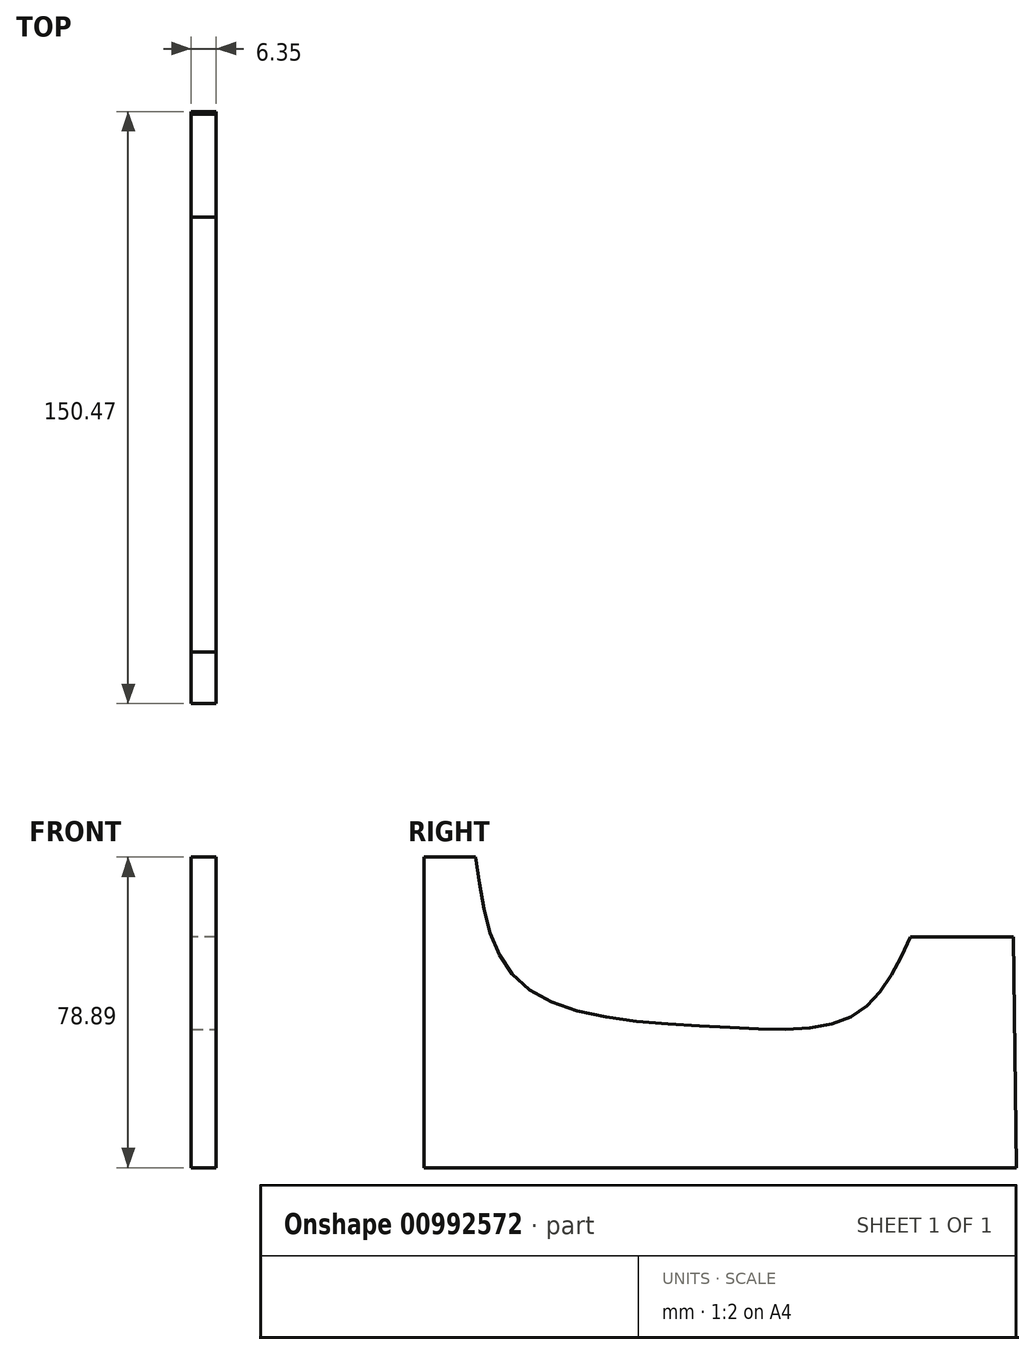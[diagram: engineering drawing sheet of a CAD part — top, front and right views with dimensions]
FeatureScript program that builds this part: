
annotation { "Feature Type Name" : "Feature", "Feature Type Description" : "" }
export const myFeature = defineFeature(function(context is Context, id is Id, definition is map)
    precondition{}
    {
        {
            var Q0;
            Q0=qCreatedBy(makeId("Right.planeOp"),FACE);
            var sketch = newSketch(context, id + "F0", { "sketchPlane" : qUnion([Q0])});
            skLineSegment(sketch, "E0", {"start": v(-73.78, 0) * mm, "end": v(-73.78, -78.89) * mm});
            skLineSegment(sketch, "E1", {"start": v(-73.78, -78.89) * mm, "end": v(76.69, -78.89) * mm});
            skLineSegment(sketch, "E2", {"start": v(76.69, -78.89) * mm, "end": v(75.96, -20.29) * mm});
            skLineSegment(sketch, "E3", {"start": v(-73.78, 0) * mm, "end": v(-60.64, 0) * mm});
            skFitSpline(sketch, "E4", {"points": [v(-60.64, 0) * mm, v(-48.52, -32.52) * mm, v(0, -43.1) * mm, v(35.81, -39.92) * mm, v(49.82, -20.29) * mm], "startDerivative": vector(20.48, -153.5) * mm, "endDerivative": vector(53.24, 113.96) * mm});
            skLineSegment(sketch, "E5", {"start": v(75.96, -20.29) * mm, "end": v(49.82, -20.29) * mm});
            skSolve(sketch);
        }
        {
            var Q0;
            Q0 = qSketchRegion(id + "F0", true);
            extrude(context, id + "F1", {"entities" : qUnion([Q0]), "depth" : 6.35 * mm, "offsetDistance" : 25.4 * mm});
        }
    });
